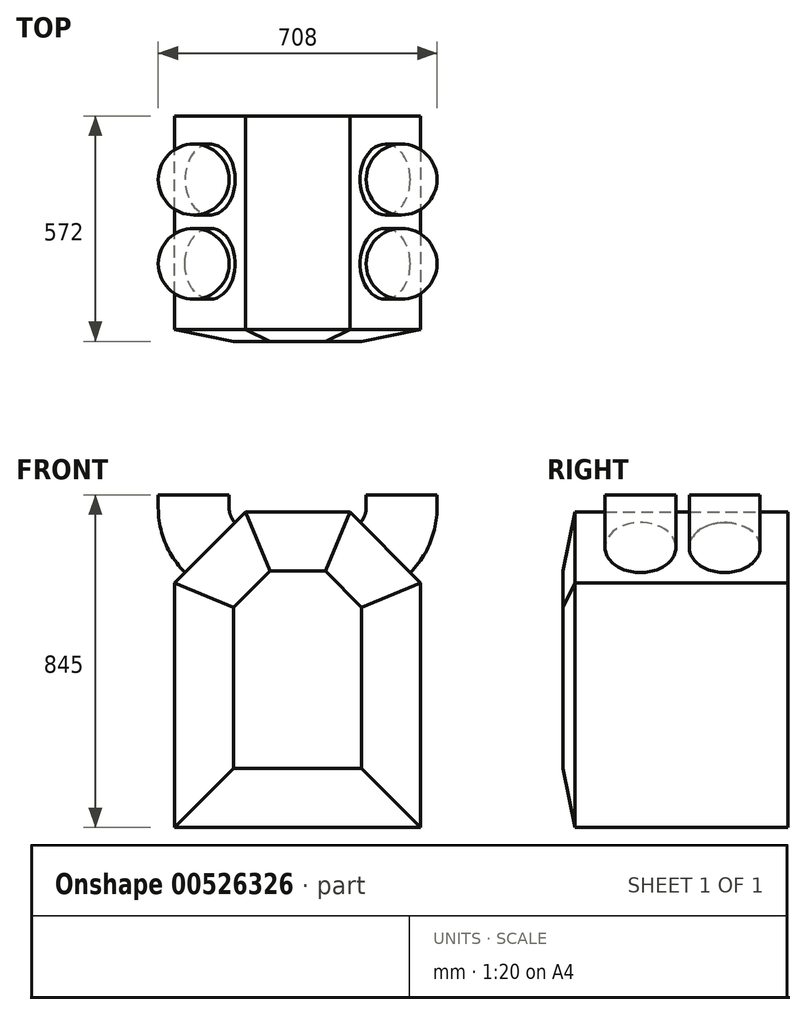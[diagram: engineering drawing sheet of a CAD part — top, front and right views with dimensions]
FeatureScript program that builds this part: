
annotation { "Feature Type Name" : "Feature", "Feature Type Description" : "" }
export const myFeature = defineFeature(function(context is Context, id is Id, definition is map)
    precondition{}
    {
        {
            var Q0;
            Q0=qCreatedBy(makeId("Front.planeOp"),FACE);
            var sketch = newSketch(context, id + "F0", { "sketchPlane" : qUnion([Q0])});
            skLineSegment(sketch, "E0.bottom", {"start": v(-312.5, 0) * mm, "end": v(312.5, 0) * mm});
            skLineSegment(sketch, "E0.top", {"start": v(-312.5, 801) * mm, "end": v(312.5, 801) * mm});
            skLineSegment(sketch, "E0.left", {"start": v(-312.5, 0) * mm, "end": v(-312.5, 801) * mm});
            skLineSegment(sketch, "E0.right", {"start": v(312.5, 0) * mm, "end": v(312.5, 801) * mm});
            skSolve(sketch);
        }
        {
            var Q0;
            Q0=makeQuery(id+"F0.imprint","IMPRINT",FACE,{"disambiguationData":[TD([[makeQuery(id+"F0.imprint","IMPRINT",EDGE,{"derivedFrom":sQuery(id+"F0.wireOp",EDGE,"E0.bottom")}),1.0]])]});
            extrude(context, id + "F1", {"entities" : qUnion([Q0]), "depth" : 572 * mm, "offsetDistance" : 25 * mm});
        }
        {
            var Q0;
            Q0=makeQuery(id+"F1.opExtrude","SWEPT_EDGE",EDGE,{"disambiguationData":[OSD([sQuery(id+"F0.wireOp",EDGE,"E0.top"),sQuery(id+"F0.wireOp",EDGE,"E0.left")])]});
            var Q1;
            Q1=makeQuery(id+"F1.opExtrude","SWEPT_EDGE",EDGE,{"disambiguationData":[OSD([sQuery(id+"F0.wireOp",EDGE,"E0.top"),sQuery(id+"F0.wireOp",EDGE,"E0.right")])]});
            chamfer(context, id + "F2", {"entities" : qUnion([Q0, Q1]), "width" : 180 * mm, "tangentPropagation" : true});
        }
        {
            var Q0;
            Q0=qCreatedBy(makeId("Top.planeOp"),FACE);
            cPlane(context, id + "F3", {"entities" : qUnion([Q0]), "cplaneType" : CPlaneType.OFFSET, "offset" : 845 * mm, "width" : 150 * mm, "height" : 150 * mm});
        }
        {
            var Q0;
            Q0=qCreatedBy(id+"F3.planeOp",FACE);
            var sketch = newSketch(context, id + "F4", { "sketchPlane" : qUnion([Q0])});
            skCircle(sketch, "E1", {"center": v(264, -161) * mm, "radius": 90 * mm});
            skCircle(sketch, "E2", {"center": v(264, -375) * mm, "radius": 90 * mm});
            skCircle(sketch, "E3", {"center": v(-264, -161) * mm, "radius": 90 * mm});
            skCircle(sketch, "E4", {"center": v(-264, -375) * mm, "radius": 90 * mm});
            skSolve(sketch);
        }
        {
            var Q0;
            Q0=makeQuery(id+"F1.opExtrude","CAP_FACE",FACE,{"disambiguationData":[OSD([sQuery(id+"F0.wireOp",EDGE,"E0.bottom"),sQuery(id+"F0.wireOp",EDGE,"E0.top"),sQuery(id+"F0.wireOp",EDGE,"E0.left"),sQuery(id+"F0.wireOp",EDGE,"E0.right")])],"isStart":true});
            var sketch = newSketch(context, id + "F5", { "sketchPlane" : qUnion([Q0])});
            skLineSegment(sketch, "E5", {"start": v(-264, 845) * mm, "end": v(-264, 811.19) * mm});
            skArc(sketch, "E6", {"start": v(-264, 811.19) * mm, "mid": v(-253.21, 756.97) * mm, "end": v(-222.5, 711) * mm});
            skLineSegment(sketch, "E7", {"start": v(0, 0) * mm, "end": v(0, 956.48) * mm, "construction": true});
            skLineSegment(sketch, "E8.MirrorCS", {"start": v(264, 845) * mm, "end": v(264, 811.19) * mm});
            skArc(sketch, "E9.MirrorCS", {"start": v(264, 811.19) * mm, "mid": v(253.21, 756.97) * mm, "end": v(222.5, 711) * mm});
            skSolve(sketch);
        }
        {
            var Q0;
            Q0=makeQuery(id+"F4.imprint","IMPRINT",FACE,{"disambiguationData":[TD([[makeQuery(id+"F4.imprint","IMPRINT",EDGE,{"derivedFrom":sQuery(id+"F4.wireOp",EDGE,"E1")}),1.0]])]});
            var Q1;
            Q1=makeQuery(id+"F4.imprint","IMPRINT",FACE,{"disambiguationData":[TD([[makeQuery(id+"F4.imprint","IMPRINT",EDGE,{"derivedFrom":sQuery(id+"F4.wireOp",EDGE,"E2")}),1.0]])]});
            var Q2;
            Q2=sQuery(id+"F5.wireOp",EDGE,"E5");
            var Q3;
            Q3=sQuery(id+"F5.wireOp",EDGE,"E6");
            sweep(context, id + "F6", {"operationType" : NewBodyOperationType.ADD, "profiles" : qUnion([Q0, Q1]), "path" : qUnion([Q2, Q3])});
        }
        {
            var Q0;
            Q0=makeQuery(id+"F4.imprint","IMPRINT",FACE,{"disambiguationData":[TD([[makeQuery(id+"F4.imprint","IMPRINT",EDGE,{"derivedFrom":sQuery(id+"F4.wireOp",EDGE,"E4")}),1.0]])]});
            var Q1;
            Q1=makeQuery(id+"F4.imprint","IMPRINT",FACE,{"disambiguationData":[TD([[makeQuery(id+"F4.imprint","IMPRINT",EDGE,{"derivedFrom":sQuery(id+"F4.wireOp",EDGE,"E3")}),1.0]])]});
            var Q2;
            Q2=sQuery(id+"F5.wireOp",EDGE,"E8.MirrorCS");
            var Q3;
            Q3=sQuery(id+"F5.wireOp",EDGE,"E9.MirrorCS");
            sweep(context, id + "F7", {"operationType" : NewBodyOperationType.ADD, "profiles" : qUnion([Q0, Q1]), "path" : qUnion([Q2, Q3])});
        }
        {
            var Q0;
            Q0=makeQuery(id+"F1.opExtrude","CAP_FACE",FACE,{"disambiguationData":[OSD([sQuery(id+"F0.wireOp",EDGE,"E0.bottom"),sQuery(id+"F0.wireOp",EDGE,"E0.top"),sQuery(id+"F0.wireOp",EDGE,"E0.left"),sQuery(id+"F0.wireOp",EDGE,"E0.right")])],"isStart":false});
            chamfer(context, id + "F8", {"entities" : qUnion([Q0]), "chamferType" : ChamferType.TWO_OFFSETS, "width1" : 30 * mm, "oppositeDirection" : true, "width2" : 150 * mm, "tangentPropagation" : true});
        }
    });
